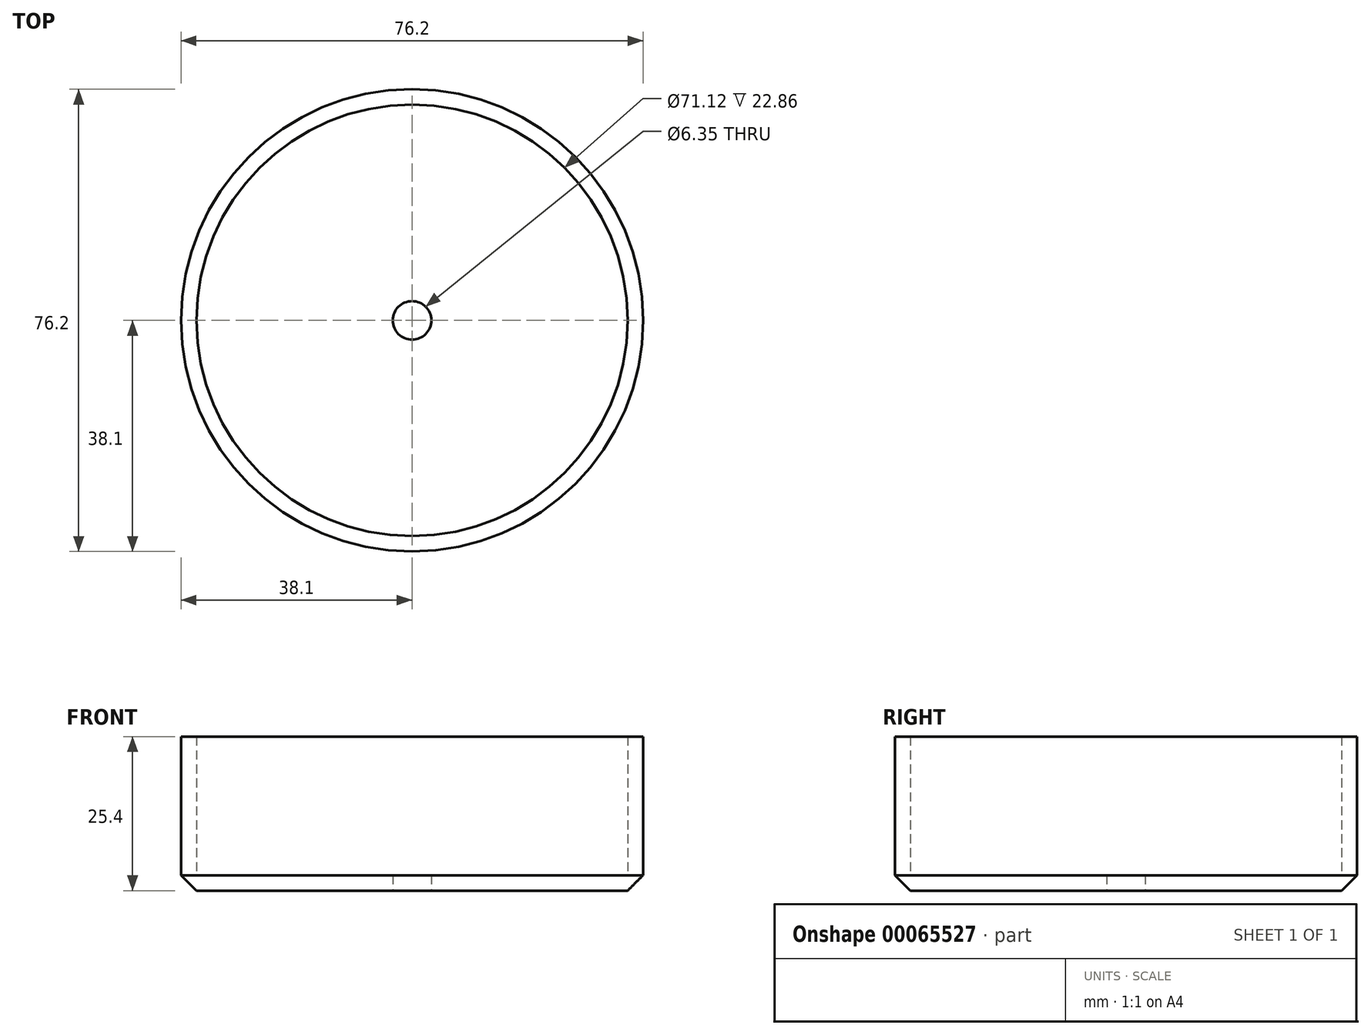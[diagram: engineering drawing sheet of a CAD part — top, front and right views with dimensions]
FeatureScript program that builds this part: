
annotation { "Feature Type Name" : "Feature", "Feature Type Description" : "" }
export const myFeature = defineFeature(function(context is Context, id is Id, definition is map)
    precondition{}
    {
        {
            var Q0;
            Q0=qCreatedBy(makeId("Top.planeOp"),FACE);
            var sketch = newSketch(context, id + "F0", { "sketchPlane" : qUnion([Q0])});
            skCircle(sketch, "E0", {"center": v(0, 0) * mm, "radius": 38.1 * mm});
            skSolve(sketch);
        }
        {
            var Q0;
            Q0 = qSketchRegion(id + "F0", true);
            extrude(context, id + "F1", {"entities" : qUnion([Q0]), "depth" : 25.4 * mm});
        }
        {
            var Q0;
            Q0=makeQuery(id+"F1.opExtrude","CAP_FACE",FACE,{"disambiguationData":[OSD([sQuery(id+"F0.wireOp",EDGE,"E0")])],"isStart":false});
            shell(context, id + "F2", {"entities" : qUnion([Q0]), "thickness" : 2.54 * mm});
        }
        {
            var Q0;
            Q0=makeQuery(id+"F1.opExtrude","CAP_FACE",FACE,{"disambiguationData":[OSD([sQuery(id+"F0.wireOp",EDGE,"E0")])],"isStart":true});
            chamfer(context, id + "F3", {"entities" : qUnion([Q0]), "width" : 2.54 * mm, "tangentPropagation" : true});
        }
        {
            var Q0;
            Q0=makeQuery(id+"F1.opExtrude","CAP_FACE",FACE,{"disambiguationData":[OSD([sQuery(id+"F0.wireOp",EDGE,"E0")])],"isStart":true});
            var sketch = newSketch(context, id + "F4", { "sketchPlane" : qUnion([Q0])});
            skPoint(sketch, "E1", {"position": v(0, 0) * mm});
            skSolve(sketch);
        }
        {
            var Q0;
            Q0=sQuery(id+"F4.wireOp",VERTEX,"E1");
            var Q1;
            Q1=makeQuery(id+"F1.opExtrude","SWEPT_BODY",BODY,{"disambiguationData":[OSD([sQuery(id+"F0.wireOp",EDGE,"E0")])]});
            hole(context, id + "F5", {"style" : HoleStyle.SIMPLE, "holeDiameter" : 6.35 * mm, "endStyle" : HoleEndStyle.THROUGH, "locations" : qUnion([Q0]), "scope" : qUnion([Q1])});
        }
    });
